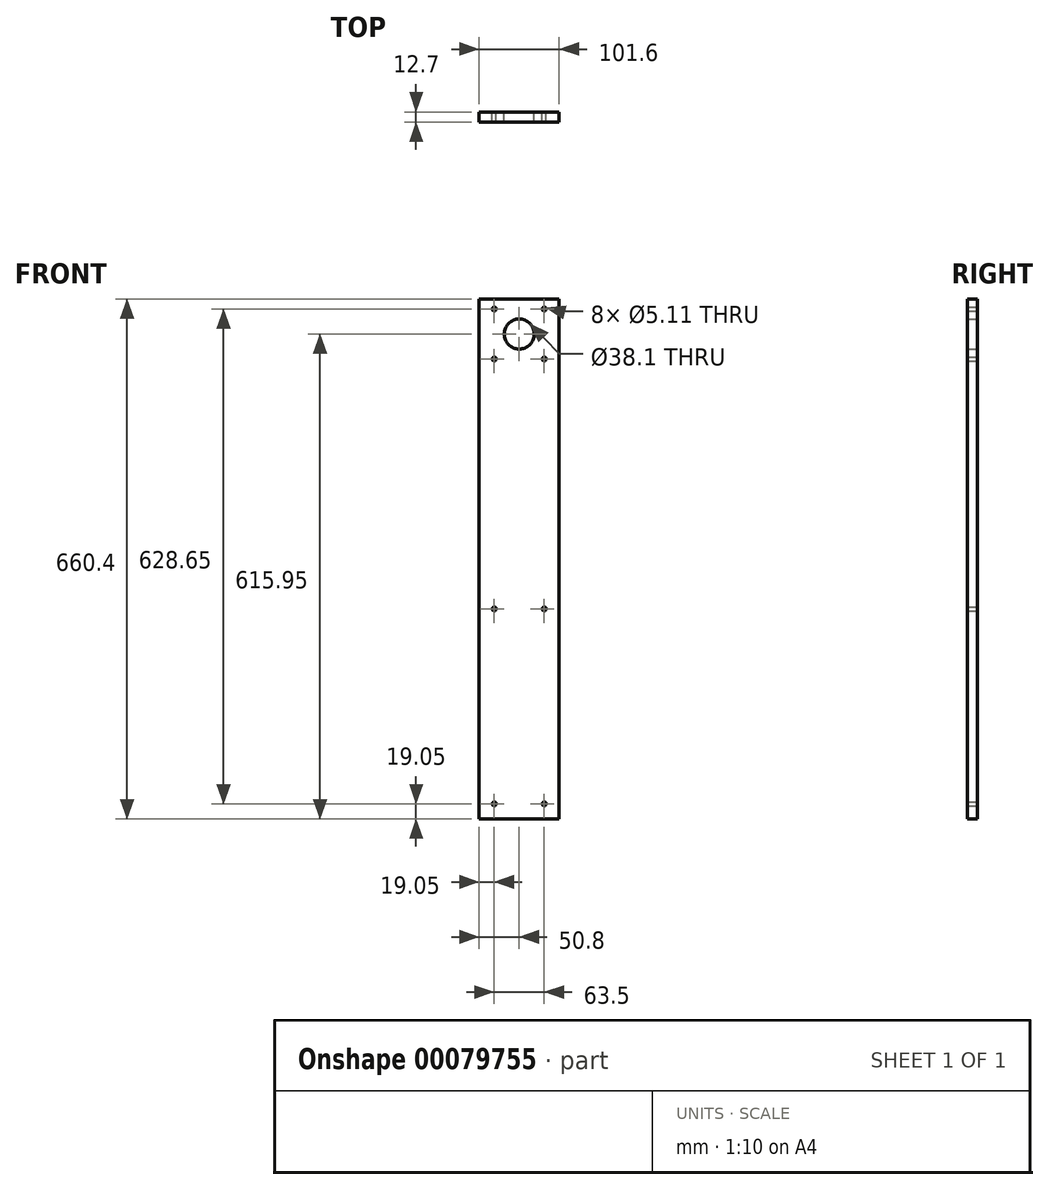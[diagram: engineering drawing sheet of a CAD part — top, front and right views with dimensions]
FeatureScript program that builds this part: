
annotation { "Feature Type Name" : "Feature", "Feature Type Description" : "" }
export const myFeature = defineFeature(function(context is Context, id is Id, definition is map)
    precondition{}
    {
        {
            var Q0;
            Q0=qCreatedBy(makeId("Front.planeOp"),FACE);
            var sketch = newSketch(context, id + "F0", { "sketchPlane" : qUnion([Q0])});
            skLineSegment(sketch, "E0.bottom", {"start": v(50.8, 330.2) * mm, "end": v(-50.8, 330.2) * mm});
            skLineSegment(sketch, "E0.top", {"start": v(50.8, -330.2) * mm, "end": v(-50.8, -330.2) * mm});
            skLineSegment(sketch, "E0.left", {"start": v(50.8, 330.2) * mm, "end": v(50.8, -330.2) * mm});
            skLineSegment(sketch, "E0.right", {"start": v(-50.8, 330.2) * mm, "end": v(-50.8, -330.2) * mm});
            skPoint(sketch, "E0.middle", {"position": v(0, 0) * mm});
            skCircle(sketch, "E1", {"center": v(31.75, -311.15) * mm, "radius": 2.55 * mm});
            skCircle(sketch, "E2", {"center": v(-31.75, -311.15) * mm, "radius": 2.55 * mm});
            skCircle(sketch, "E3", {"center": v(-31.75, -63.5) * mm, "radius": 2.55 * mm});
            skCircle(sketch, "E4", {"center": v(31.75, -63.5) * mm, "radius": 2.55 * mm});
            skCircle(sketch, "E5", {"center": v(0, 285.75) * mm, "radius": 19.05 * mm});
            skPoint(sketch, "E5.centerSnap0", {"position": v(0, 330.2) * mm});
            skCircle(sketch, "E6", {"center": v(-31.75, 317.5) * mm, "radius": 2.55 * mm});
            skCircle(sketch, "E7", {"center": v(31.75, 317.5) * mm, "radius": 2.55 * mm});
            skCircle(sketch, "E8", {"center": v(-31.75, 254) * mm, "radius": 2.55 * mm});
            skCircle(sketch, "E9", {"center": v(31.75, 254) * mm, "radius": 2.55 * mm});
            skSolve(sketch);
        }
        {
            var Q0;
            Q0 = qSketchRegion(id + "F0", true);
            extrude(context, id + "F1", {"entities" : qUnion([Q0]), "depth" : 12.7 * mm});
        }
    });
